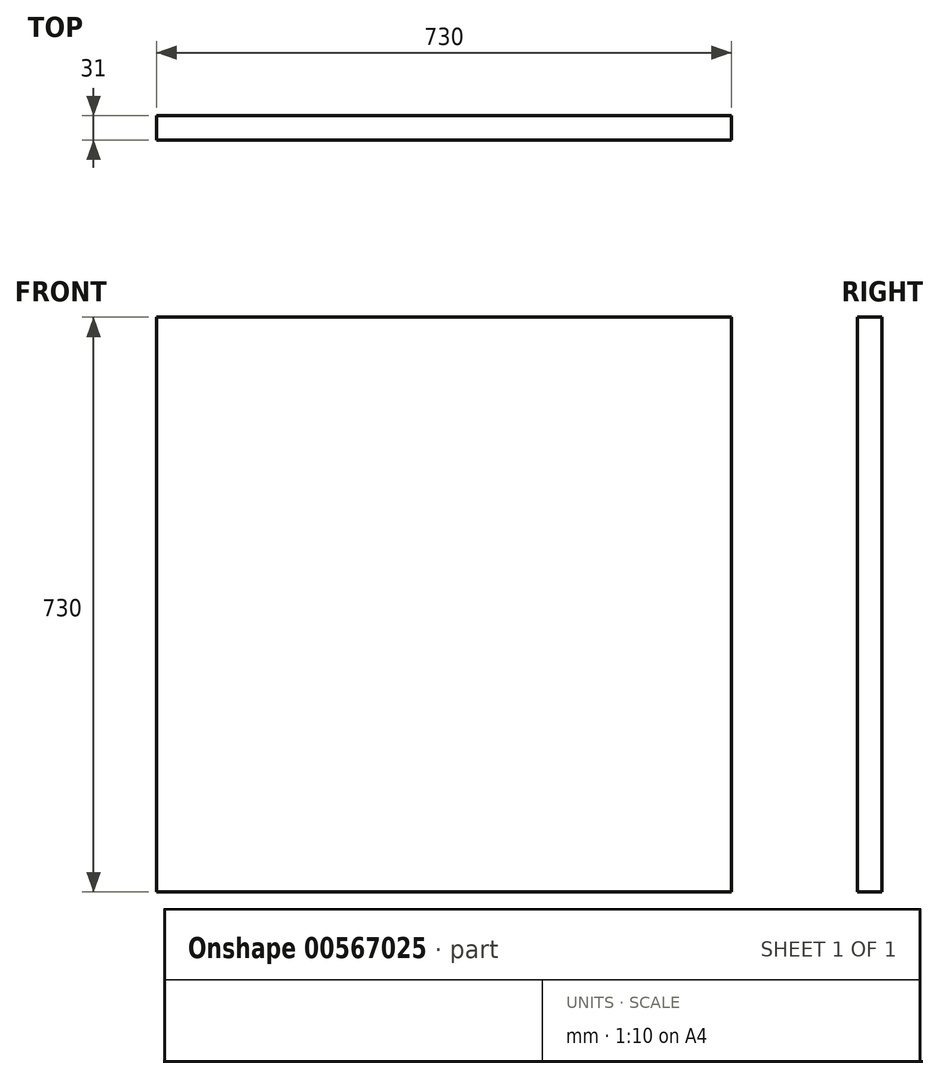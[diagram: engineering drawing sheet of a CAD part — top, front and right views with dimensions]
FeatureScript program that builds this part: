
annotation { "Feature Type Name" : "Feature", "Feature Type Description" : "" }
export const myFeature = defineFeature(function(context is Context, id is Id, definition is map)
    precondition{}
    {
        {
            var Q0;
            Q0=qCreatedBy(makeId("Front.planeOp"),FACE);
            var sketch = newSketch(context, id + "F0", { "sketchPlane" : qUnion([Q0])});
            skLineSegment(sketch, "E0.bottom", {"start": v(-782.44, 419.28) * mm, "end": v(-52.44, 419.28) * mm});
            skLineSegment(sketch, "E0.top", {"start": v(-782.44, -310.72) * mm, "end": v(-52.44, -310.72) * mm});
            skLineSegment(sketch, "E0.left", {"start": v(-782.44, 419.28) * mm, "end": v(-782.44, -310.72) * mm});
            skLineSegment(sketch, "E0.right", {"start": v(-52.44, 419.28) * mm, "end": v(-52.44, -310.72) * mm});
            skSolve(sketch);
        }
        {
            var Q0;
            Q0 = qSketchRegion(id + "F0", true);
            extrude(context, id + "F1", {"entities" : qUnion([Q0]), "depth" : 31 * mm, "offsetDistance" : 25 * mm});
        }
    });
